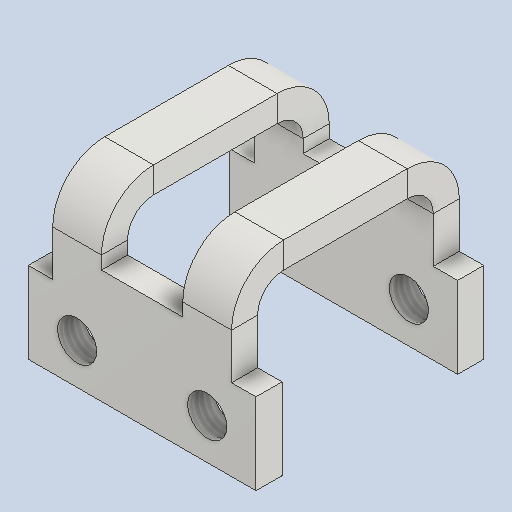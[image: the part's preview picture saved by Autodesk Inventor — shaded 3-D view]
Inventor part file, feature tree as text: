
AUTODESK INVENTOR PART (.ipt)
format: ipt  version: 2024 (Build 280153000, 153)  size: 592,384 bytes
history: native  units: mm
features: sheet_metal_op x7, thread x4, sketch x4, other x3, plane x1, mirror x1, extrude x1
ambient origin geometry x8: Origin, YZ Plane, XZ Plane, XY Plane, X Axis, Y Axis, Z Axis, Center Point
bodies: Solid1 (feature_tree)
feature tree (21):
  sheet_metal_op  "Face1"
  sheet_metal_op  "Flange1"
  plane  "Work Plane2"
  mirror  "Mirror1"
  sheet_metal_op  "Flange4"
  extrude  "Extrusion1"  Depth=8.0mm
  thread  "Thread9"  [1 undecoded]
  thread  "Thread10"  [1 undecoded]
  thread  "Thread11"  [1 undecoded]
  thread  "Thread12"  [1 undecoded]
  sketch  "Sketch1"  dims[d8=25.0mm d12=8.0mm d13=8.0mm d14=4.0mm d15=16.0mm d16=8.0mm]
  other  "Plate1"
  sketch  "Sketch2"  dims[d17=35.0mm d18=90.0deg d19=8.0mm]
  other  "Plate2"
  sheet_metal_op  "Bend1"
  sheet_metal_op  "Corner1"
  sketch  "Sketch6"  dims[d20=32.0mm]
  other  "Plate5"
  sheet_metal_op  "Bend4"
  sheet_metal_op  "Corner4"
  sketch  "Sketch7"  dims[d21=8.0mm d22=8.0mm d44=-35.0mm d45=8.0mm d46=4.0mm d47=16.0mm d48=8.0mm d49=35.0mm d50=90.0deg d51=8.0mm d52=32.0mm d53=8.0mm d54=8.0mm d55=12.0mm d56=12.0mm d57=40.0mm d61=80.0mm d62=0.0mm d116=55.0mm d128=30.0mm d129=7.5mm d130=25.0mm d131=70.0mm d132=90.0deg d133=25.0mm d134=7.5mm d135=27.5mm d136=0.0mm d137=15.0mm d138=12.5mm d139=20.0mm d140=350.0mm d141=0.0mm d142=350.0mm d143=0.0mm d144=350.0mm d145=0.0mm d146=350.0mm d147=0.0mm]
note: 4 required parameter values undecoded (feature->parameter linkage not recoverable at this tier; creation-order binding heuristic only, values carry confidence <= 0.55)
